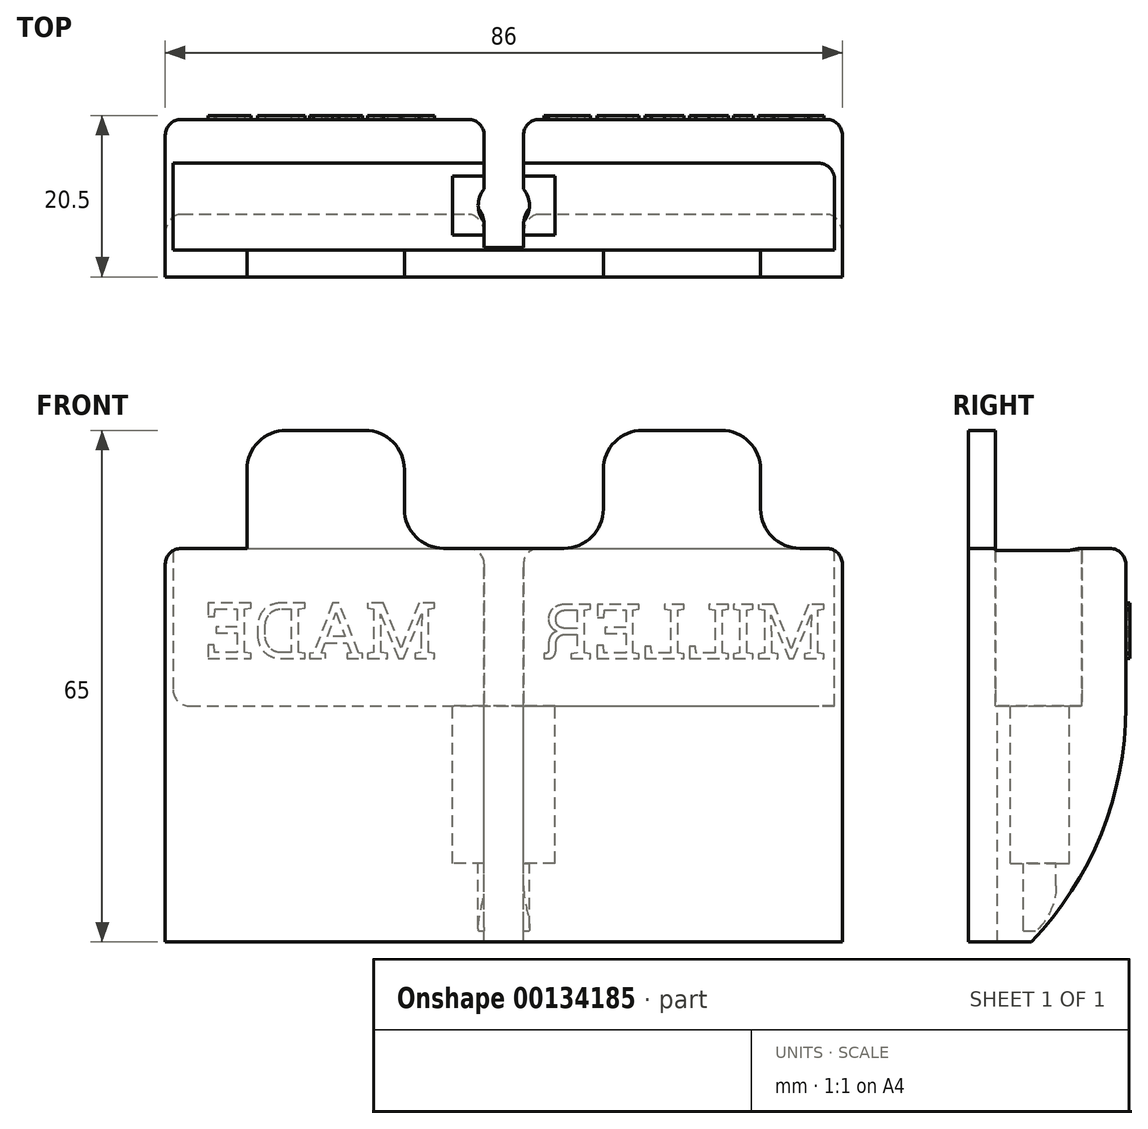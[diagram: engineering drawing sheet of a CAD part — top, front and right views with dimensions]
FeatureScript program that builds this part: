
annotation { "Feature Type Name" : "Feature", "Feature Type Description" : "" }
export const myFeature = defineFeature(function(context is Context, id is Id, definition is map)
    precondition{}
    {
        {
            var Q0;
            Q0=qCreatedBy(makeId("Top.planeOp"),FACE);
            var sketch = newSketch(context, id + "F0", { "sketchPlane" : qUnion([Q0])});
            skLineSegment(sketch, "E0.bottom", {"start": v(0, 0) * mm, "end": v(83, 0) * mm});
            skLineSegment(sketch, "E0.top", {"start": v(0, 20) * mm, "end": v(83, 20) * mm});
            skLineSegment(sketch, "E0.left", {"start": v(0, 0) * mm, "end": v(0, 20) * mm});
            skLineSegment(sketch, "E0.right", {"start": v(83, 0) * mm, "end": v(83, 20) * mm});
            skLineSegment(sketch, "E1.bottom", {"start": v(0, 5.2) * mm, "end": v(83, 5.2) * mm});
            skLineSegment(sketch, "E1.top", {"start": v(0, 16.2) * mm, "end": v(83, 16.2) * mm});
            skLineSegment(sketch, "E1.left", {"start": v(0, 5.2) * mm, "end": v(0, 16.2) * mm});
            skLineSegment(sketch, "E1.right", {"start": v(83, 5.2) * mm, "end": v(83, 16.2) * mm});
            skSolve(sketch);
        }
        {
            var Q0;
            {var subQ0=sQuery(id+"F0.wireOp",EDGE,"E0.bottom");Q0=makeQuery(id+"F0.imprint","IMPRINT",FACE,{"disambiguationData":[TD([[makeQuery(id+"F0.imprint","IMPRINT",EDGE,{"derivedFrom":subQ0}),1.0]])]});}
            var Q1;
            {var subQ0=sQuery(id+"F0.wireOp",EDGE,"E0.top");Q1=makeQuery(id+"F0.imprint","IMPRINT",FACE,{"disambiguationData":[TD([[makeQuery(id+"F0.imprint","IMPRINT",EDGE,{"derivedFrom":subQ0}),-1.0]])]});}
            var Q2;
            Q2=makeQuery(id+"F0.imprint","IMPRINT",FACE,{"disambiguationData":[TD([[makeQuery(id+"F0.imprint","IMPRINT",EDGE,{"derivedFrom":sQuery(id+"F0.wireOp",EDGE,"E1.bottom")}),1.0]])]});
            extrude(context, id + "F1", {"entities" : qUnion([Q0, Q1, Q2]), "depth" : 30 * mm});
        }
        {
            var Q0;
            Q0=makeQuery(id+"F1.opExtrude","CAP_FACE",FACE,{"disambiguationData":[OSD([sQuery(id+"F0.wireOp",EDGE,"E0.bottom"),sQuery(id+"F0.wireOp",EDGE,"E0.top"),sQuery(id+"F0.wireOp",EDGE,"E0.left"),sQuery(id+"F0.wireOp",EDGE,"E0.right"),sQuery(id+"F0.wireOp",EDGE,"E1.left"),sQuery(id+"F0.wireOp",EDGE,"E1.right")])],"isStart":false});
            var sketch = newSketch(context, id + "F2", { "sketchPlane" : qUnion([Q0])});
            skLineSegment(sketch, "E2.bottom", {"start": v(0, 3.43) * mm, "end": v(83, 3.43) * mm});
            skLineSegment(sketch, "E2.top", {"start": v(0, 14.43) * mm, "end": v(83, 14.43) * mm});
            skLineSegment(sketch, "E2.left", {"start": v(0, 3.43) * mm, "end": v(0, 14.43) * mm});
            skLineSegment(sketch, "E2.right", {"start": v(83, 3.43) * mm, "end": v(83, 14.43) * mm});
            skSolve(sketch);
        }
        {
            var Q0;
            Q0=makeQuery(id+"F2.imprint","IMPRINT",FACE,{"disambiguationData":[TD([[makeQuery(id+"F2.imprint","IMPRINT",EDGE,{"derivedFrom":sQuery(id+"F2.wireOp",EDGE,"E2.bottom")}),1.0]])]});
            extrude(context, id + "F3", {"entities" : qUnion([Q0]), "operationType" : NewBodyOperationType.REMOVE, "oppositeDirection" : true, "depth" : 15 * mm});
        }
        {
            var Q0;
            {var subQ0=sQuery(id+"F0.wireOp",EDGE,"E0.top");var subQ1=sQuery(id+"F0.wireOp",EDGE,"E1.left");var subQ2=sQuery(id+"F0.wireOp",EDGE,"E0.left");var subQ3=sQuery(id+"F0.wireOp",EDGE,"E1.right");var subQ4=sQuery(id+"F0.wireOp",EDGE,"E0.right");Q0=makeQuery(id+"F3.boolean.opBoolean","SPLIT",FACE,{"disambiguationData":[TD([makeQuery(id+"F1.opExtrude","SWEPT_FACE",FACE,{"disambiguationData":[OSD([subQ0])]})])],"derivedFrom":makeQuery(id+"F1.opExtrude","CAP_FACE",FACE,{"disambiguationData":[OSD([sQuery(id+"F0.wireOp",EDGE,"E0.bottom"),subQ0,subQ2,subQ4,subQ1,subQ3])],"isStart":false})});}
            var sketch = newSketch(context, id + "F4", { "sketchPlane" : qUnion([Q0])});
            skLineSegment(sketch, "E3", {"start": v(41.5, 20) * mm, "end": v(41.5, -12.57) * mm, "construction": true});
            skLineSegment(sketch, "E4.bottom", {"start": v(44, 3.71) * mm, "end": v(39, 3.71) * mm});
            skLineSegment(sketch, "E4.top", {"start": v(44, 36.29) * mm, "end": v(39, 36.29) * mm});
            skLineSegment(sketch, "E4.left", {"start": v(44, 3.71) * mm, "end": v(44, 36.29) * mm});
            skLineSegment(sketch, "E4.right", {"start": v(39, 3.71) * mm, "end": v(39, 36.29) * mm});
            skPoint(sketch, "E4.middle", {"position": v(41.5, 20) * mm});
            skPoint(sketch, "E4.cornerSnap0", {"position": v(41.5, 3.71) * mm});
            skSolve(sketch);
        }
        {
            var Q0;
            {var subQ0=sQuery(id+"F4.wireOp",EDGE,"E4.bottom");Q0=makeQuery(id+"F4.imprint","IMPRINT",FACE,{"disambiguationData":[TD([[makeQuery(id+"F4.imprint","IMPRINT",EDGE,{"derivedFrom":subQ0}),-1.0]])]});}
            var Q1;
            {var subQ0=sQuery(id+"F4.wireOp",EDGE,"E4.left");var subQ1=makeQuery(id+"F3.boolean.opBoolean","COPY",EDGE,{"derivedFrom":makeQuery(id+"F3.opExtrude","CAP_EDGE",EDGE,{"disambiguationData":[OSD([sQuery(id+"F2.wireOp",EDGE,"E2.top")])],"isStart":true})});var subQ2=makeQuery(id+"F4.imprint","INTERSECT",VERTEX,{"derivedFrom":[subQ1,subQ0]});Q1=makeQuery(id+"F4.imprint","IMPRINT",FACE,{"disambiguationData":[TD([[makeQuery(id+"F4.imprint","IMPRINT",EDGE,{"disambiguationData":[TD([[subQ2,-1.0]])],"derivedFrom":subQ0}),1.0]])]});}
            var Q2;
            {var subQ0=sQuery(id+"F4.wireOp",EDGE,"E4.top");Q2=makeQuery(id+"F4.imprint","IMPRINT",FACE,{"disambiguationData":[TD([[makeQuery(id+"F4.imprint","IMPRINT",EDGE,{"derivedFrom":subQ0}),1.0]])]});}
            extrude(context, id + "F5", {"entities" : qUnion([Q0, Q1, Q2]), "operationType" : NewBodyOperationType.REMOVE, "oppositeDirection" : true, "depth" : 77.48 * mm});
        }
        {
            var Q0;
            Q0=makeQuery(id+"F3.boolean.opBoolean","COPY",FACE,{"derivedFrom":makeQuery(id+"F3.opExtrude","CAP_FACE",FACE,{"disambiguationData":[OSD([sQuery(id+"F2.wireOp",EDGE,"E2.bottom"),sQuery(id+"F2.wireOp",EDGE,"E2.top"),sQuery(id+"F2.wireOp",EDGE,"E2.left"),sQuery(id+"F2.wireOp",EDGE,"E2.right")])],"isStart":false})});
            var sketch = newSketch(context, id + "F6", { "sketchPlane" : qUnion([Q0])});
            skLineSegment(sketch, "E5", {"start": v(44, 14.43) * mm, "end": v(39, 14.43) * mm, "construction": true});
            skLineSegment(sketch, "E6", {"start": v(41.5, 14.43) * mm, "end": v(41.5, 3.71) * mm, "construction": true});
            skLineSegment(sketch, "E7.bottom", {"start": v(48, 5.32) * mm, "end": v(35, 5.32) * mm});
            skLineSegment(sketch, "E7.top", {"start": v(48, 12.82) * mm, "end": v(35, 12.82) * mm});
            skLineSegment(sketch, "E7.left", {"start": v(48, 5.32) * mm, "end": v(48, 12.82) * mm});
            skLineSegment(sketch, "E7.right", {"start": v(35, 5.32) * mm, "end": v(35, 12.82) * mm});
            skPoint(sketch, "E7.middle", {"position": v(41.5, 9.07) * mm});
            skSolve(sketch);
        }
        {
            var Q0;
            Q0=makeQuery(id+"F1.opExtrude","CAP_FACE",FACE,{"disambiguationData":[OSD([sQuery(id+"F0.wireOp",EDGE,"E0.bottom"),sQuery(id+"F0.wireOp",EDGE,"E0.top"),sQuery(id+"F0.wireOp",EDGE,"E0.left"),sQuery(id+"F0.wireOp",EDGE,"E0.right"),sQuery(id+"F0.wireOp",EDGE,"E1.left"),sQuery(id+"F0.wireOp",EDGE,"E1.right")])],"isStart":true});
            extrude(context, id + "F7", {"entities" : qUnion([Q0]), "operationType" : NewBodyOperationType.ADD, "depth" : 15 * mm});
        }
        {
            var Q0;
            {var subQ0=sQuery(id+"F6.wireOp",EDGE,"E7.left");Q0=makeQuery(id+"F6.imprint","IMPRINT",FACE,{"disambiguationData":[TD([[makeQuery(id+"F6.imprint","IMPRINT",EDGE,{"derivedFrom":subQ0}),1.0]])]});}
            var Q1;
            {var subQ0=sQuery(id+"F6.wireOp",EDGE,"E7.right");Q1=makeQuery(id+"F6.imprint","IMPRINT",FACE,{"disambiguationData":[TD([[makeQuery(id+"F6.imprint","IMPRINT",EDGE,{"derivedFrom":subQ0}),-1.0]])]});}
            extrude(context, id + "F8", {"entities" : qUnion([Q0, Q1]), "operationType" : NewBodyOperationType.REMOVE, "oppositeDirection" : true, "depth" : 20 * mm});
        }
        {
            var Q0;
            {var subQ2=sQuery(id+"F0.wireOp",EDGE,"E0.top");Q0=makeQuery(id+"F7.opExtrude","CAP_EDGE",EDGE,{"disambiguationData":[OSD([subQ2]),TDD([makeQuery(id+"F5.boolean.opBoolean","SPLIT",EDGE,{"disambiguationData":[TD([makeQuery(id+"F5.opExtrude","SWEPT_FACE",FACE,{"disambiguationData":[OSD([sQuery(id+"F4.wireOp",EDGE,"E4.left")])]})])],"derivedFrom":makeQuery(id+"F1.opExtrude","CAP_EDGE",EDGE,{"disambiguationData":[OSD([subQ2])],"isStart":true})})])],"isStart":false});}
            var Q1;
            {var subQ2=sQuery(id+"F0.wireOp",EDGE,"E0.top");Q1=makeQuery(id+"F7.opExtrude","CAP_EDGE",EDGE,{"disambiguationData":[OSD([subQ2]),TDD([makeQuery(id+"F5.boolean.opBoolean","SPLIT",EDGE,{"disambiguationData":[TD([makeQuery(id+"F5.opExtrude","SWEPT_FACE",FACE,{"disambiguationData":[OSD([sQuery(id+"F4.wireOp",EDGE,"E4.right")])]})])],"derivedFrom":makeQuery(id+"F1.opExtrude","CAP_EDGE",EDGE,{"disambiguationData":[OSD([subQ2])],"isStart":true})})])],"isStart":false});}
            chamfer(context, id + "F9", {"entities" : qUnion([Q0, Q1]), "width" : 12 * mm, "tangentPropagation" : true});
        }
        {
            var Q0;
            {var subQ4=sQuery(id+"F0.wireOp",EDGE,"E0.top");var subQ7=makeQuery(id+"F1.opExtrude","SWEPT_FACE",FACE,{"disambiguationData":[OSD([subQ4])]});var subQ9=makeQuery(id+"F5.opExtrude","SWEPT_FACE",FACE,{"disambiguationData":[OSD([sQuery(id+"F4.wireOp",EDGE,"E4.left")])]});var subQ10=makeQuery(id+"F5.boolean.opBoolean","SPLIT",EDGE,{"disambiguationData":[TD([subQ9])],"derivedFrom":makeQuery(id+"F1.opExtrude","CAP_EDGE",EDGE,{"disambiguationData":[OSD([subQ4])],"isStart":true})});Q0=makeQuery(id+"F9.opChamfer","BLEND_EDGE",EDGE,{"blendedFrom":[makeQuery(id+"F7.opExtrude","CAP_EDGE",EDGE,{"disambiguationData":[OSD([subQ4]),TDD([subQ10])],"isStart":false}),makeQuery(id+"F7.boolean.opBoolean","MERGE",FACE,{"derivedFrom":[makeQuery(id+"F5.boolean.opBoolean","SPLIT",FACE,{"disambiguationData":[TD([subQ9])],"derivedFrom":subQ7}),makeQuery(id+"F7.opExtrude","SWEPT_FACE",FACE,{"disambiguationData":[OSD([subQ4]),TDD([subQ10])]})]})],"blendedInto":[makeQuery(id+"F7.boolean.opBoolean","MERGE",FACE,{"derivedFrom":[makeQuery(id+"F5.boolean.opBoolean","SPLIT",FACE,{"disambiguationData":[TD([subQ9])],"derivedFrom":subQ7}),makeQuery(id+"F7.opExtrude","SWEPT_FACE",FACE,{"disambiguationData":[OSD([subQ4]),TDD([subQ10])]})]})]});}
            var Q1;
            {var subQ4=sQuery(id+"F0.wireOp",EDGE,"E0.top");var subQ7=makeQuery(id+"F1.opExtrude","SWEPT_FACE",FACE,{"disambiguationData":[OSD([subQ4])]});var subQ9=makeQuery(id+"F5.opExtrude","SWEPT_FACE",FACE,{"disambiguationData":[OSD([sQuery(id+"F4.wireOp",EDGE,"E4.right")])]});var subQ10=makeQuery(id+"F5.boolean.opBoolean","SPLIT",EDGE,{"disambiguationData":[TD([subQ9])],"derivedFrom":makeQuery(id+"F1.opExtrude","CAP_EDGE",EDGE,{"disambiguationData":[OSD([subQ4])],"isStart":true})});Q1=makeQuery(id+"F9.opChamfer","BLEND_EDGE",EDGE,{"blendedFrom":[makeQuery(id+"F7.opExtrude","CAP_EDGE",EDGE,{"disambiguationData":[OSD([subQ4]),TDD([subQ10])],"isStart":false}),makeQuery(id+"F7.boolean.opBoolean","MERGE",FACE,{"derivedFrom":[makeQuery(id+"F5.boolean.opBoolean","SPLIT",FACE,{"disambiguationData":[TD([subQ9])],"derivedFrom":subQ7}),makeQuery(id+"F7.opExtrude","SWEPT_FACE",FACE,{"disambiguationData":[OSD([subQ4]),TDD([subQ10])]})]})],"blendedInto":[makeQuery(id+"F7.boolean.opBoolean","MERGE",FACE,{"derivedFrom":[makeQuery(id+"F5.boolean.opBoolean","SPLIT",FACE,{"disambiguationData":[TD([subQ9])],"derivedFrom":subQ7}),makeQuery(id+"F7.opExtrude","SWEPT_FACE",FACE,{"disambiguationData":[OSD([subQ4]),TDD([subQ10])]})]})]});}
            fillet(context, id + "F10", {"entities" : qUnion([Q0, Q1]), "radius" : 42.96 * mm, "tangentPropagation" : true, "allowEdgeOverflow" : false});
        }
        {
            var Q0;
            {var subQ4=sQuery(id+"F0.wireOp",EDGE,"E0.top");var subQ7=makeQuery(id+"F1.opExtrude","SWEPT_FACE",FACE,{"disambiguationData":[OSD([subQ4])]});var subQ9=makeQuery(id+"F5.opExtrude","SWEPT_FACE",FACE,{"disambiguationData":[OSD([sQuery(id+"F4.wireOp",EDGE,"E4.left")])]});Q0=makeQuery(id+"F7.boolean.opBoolean","MERGE",FACE,{"derivedFrom":[makeQuery(id+"F5.boolean.opBoolean","SPLIT",FACE,{"disambiguationData":[TD([subQ9])],"derivedFrom":subQ7}),makeQuery(id+"F7.opExtrude","SWEPT_FACE",FACE,{"disambiguationData":[OSD([subQ4]),TDD([makeQuery(id+"F5.boolean.opBoolean","SPLIT",EDGE,{"disambiguationData":[TD([subQ9])],"derivedFrom":makeQuery(id+"F1.opExtrude","CAP_EDGE",EDGE,{"disambiguationData":[OSD([subQ4])],"isStart":true})})])]})]});}
            var sketch = newSketch(context, id + "F11", { "sketchPlane" : qUnion([Q0])});
            skText(sketch, "E8", { "text": "MILLER", "fontName": "Arimo-Regular.ttf"});
            skPoint(sketch, "E9", {"position": v(-63.5, 30) * mm});
            skText(sketch, "E10", { "text": "MADE", "fontName": "DroidSansMono.ttf"});
            const initialGuessF11  = {"E8": [-0.07876, 0.02007, 1, 0, 0.00604], "E10": [-0.03074, 0.02007, 1, 0, 0.00604]};
            skSetInitialGuess(sketch, initialGuessF11);
            skSolve(sketch);
        }
        {
            var Q0;
            Q0 = qSketchRegion(id + "F11", true);
            extrude(context, id + "F12", {"entities" : qUnion([Q0]), "operationType" : NewBodyOperationType.ADD, "oppositeDirection" : true, "depth" : 1 * mm});
        }
        {
            var Q0;
            {var subQ0=sQuery(id+"F0.wireOp",EDGE,"E0.bottom");var subQ1=sQuery(id+"F0.wireOp",EDGE,"E1.left");var subQ2=sQuery(id+"F0.wireOp",EDGE,"E0.left");var subQ3=sQuery(id+"F0.wireOp",EDGE,"E1.right");var subQ4=sQuery(id+"F0.wireOp",EDGE,"E0.right");Q0=makeQuery(id+"F3.boolean.opBoolean","SPLIT",FACE,{"disambiguationData":[TD([makeQuery(id+"F1.opExtrude","SWEPT_FACE",FACE,{"disambiguationData":[OSD([subQ0])]})])],"derivedFrom":makeQuery(id+"F1.opExtrude","CAP_FACE",FACE,{"disambiguationData":[OSD([subQ0,sQuery(id+"F0.wireOp",EDGE,"E0.top"),subQ2,subQ4,subQ1,subQ3])],"isStart":false})});}
            var Q1;
            {var subQ0=sQuery(id+"F0.wireOp",EDGE,"E0.top");var subQ1=makeQuery(id+"F1.opExtrude","SWEPT_FACE",FACE,{"disambiguationData":[OSD([subQ0])]});var subQ2=sQuery(id+"F0.wireOp",EDGE,"E1.right");var subQ3=sQuery(id+"F0.wireOp",EDGE,"E0.right");var subQ6=sQuery(id+"F0.wireOp",EDGE,"E1.left");var subQ7=sQuery(id+"F0.wireOp",EDGE,"E0.left");Q1=makeQuery(id+"F5.boolean.opBoolean","SPLIT",FACE,{"disambiguationData":[TD([makeQuery(id+"F5.opExtrude","SWEPT_FACE",FACE,{"disambiguationData":[OSD([sQuery(id+"F4.wireOp",EDGE,"E4.left")])]})])],"derivedFrom":makeQuery(id+"F3.boolean.opBoolean","SPLIT",FACE,{"disambiguationData":[TD([subQ1])],"derivedFrom":makeQuery(id+"F1.opExtrude","CAP_FACE",FACE,{"disambiguationData":[OSD([sQuery(id+"F0.wireOp",EDGE,"E0.bottom"),subQ0,subQ7,subQ3,subQ6,subQ2])],"isStart":false})})});}
            var Q2;
            {var subQ0=sQuery(id+"F0.wireOp",EDGE,"E0.top");var subQ1=makeQuery(id+"F1.opExtrude","SWEPT_FACE",FACE,{"disambiguationData":[OSD([subQ0])]});var subQ2=sQuery(id+"F0.wireOp",EDGE,"E1.left");var subQ3=sQuery(id+"F0.wireOp",EDGE,"E0.left");var subQ6=sQuery(id+"F0.wireOp",EDGE,"E1.right");var subQ7=sQuery(id+"F0.wireOp",EDGE,"E0.right");Q2=makeQuery(id+"F5.boolean.opBoolean","SPLIT",FACE,{"disambiguationData":[TD([makeQuery(id+"F5.opExtrude","SWEPT_FACE",FACE,{"disambiguationData":[OSD([sQuery(id+"F4.wireOp",EDGE,"E4.right")])]})])],"derivedFrom":makeQuery(id+"F3.boolean.opBoolean","SPLIT",FACE,{"disambiguationData":[TD([subQ1])],"derivedFrom":makeQuery(id+"F1.opExtrude","CAP_FACE",FACE,{"disambiguationData":[OSD([sQuery(id+"F0.wireOp",EDGE,"E0.bottom"),subQ0,subQ3,subQ7,subQ2,subQ6])],"isStart":false})})});}
            extrude(context, id + "F13", {"entities" : qUnion([Q0, Q1, Q2]), "operationType" : NewBodyOperationType.ADD, "depth" : 5 * mm});
        }
        {
            var Q0;
            Q0=makeQuery(id+"F8.boolean.opBoolean","COPY",FACE,{"derivedFrom":makeQuery(id+"F8.opExtrude","CAP_FACE",FACE,{"disambiguationData":[OSD([sQuery(id+"F2.wireOp",EDGE,"E2.bottom"),sQuery(id+"F2.wireOp",EDGE,"E2.top"),sQuery(id+"F2.wireOp",EDGE,"E2.left"),sQuery(id+"F2.wireOp",EDGE,"E2.right"),sQuery(id+"F4.wireOp",EDGE,"E4.left"),sQuery(id+"F6.wireOp",EDGE,"E7.bottom"),sQuery(id+"F6.wireOp",EDGE,"E7.top"),sQuery(id+"F6.wireOp",EDGE,"E7.left")])],"isStart":false})});
            var sketch = newSketch(context, id + "F14", { "sketchPlane" : qUnion([Q0])});
            skLineSegment(sketch, "E11", {"start": v(48, 9.07) * mm, "end": v(35, 9.07) * mm, "construction": true});
            skCircle(sketch, "E12", {"center": v(41.5, 9.07) * mm, "radius": 3.25 * mm});
            skSolve(sketch);
        }
        {
            var Q0;
            {var subQ0=sQuery(id+"F14.wireOp",EDGE,"E12");var subQ1=makeQuery(id+"F8.boolean.opBoolean","COPY",EDGE,{"derivedFrom":makeQuery(id+"F8.opExtrude","CAP_EDGE",EDGE,{"disambiguationData":[OSD([sQuery(id+"F2.wireOp",EDGE,"E2.bottom"),sQuery(id+"F2.wireOp",EDGE,"E2.top"),sQuery(id+"F2.wireOp",EDGE,"E2.left"),sQuery(id+"F2.wireOp",EDGE,"E2.right"),sQuery(id+"F4.wireOp",EDGE,"E4.left")])],"isStart":false})});var subQ2=makeQuery(id+"F14.imprint","INTERSECT",VERTEX,{"disambiguationData":[OD(0.0)],"derivedFrom":[subQ1,subQ0]});Q0=makeQuery(id+"F14.imprint","IMPRINT",FACE,{"disambiguationData":[TD([[makeQuery(id+"F14.imprint","IMPRINT",EDGE,{"disambiguationData":[TD([[subQ2,-1.0]])],"derivedFrom":subQ0}),1.0]])]});}
            var Q1;
            {var subQ0=sQuery(id+"F14.wireOp",EDGE,"E12");var subQ1=makeQuery(id+"F8.boolean.opBoolean","COPY",EDGE,{"derivedFrom":makeQuery(id+"F8.opExtrude","CAP_EDGE",EDGE,{"disambiguationData":[OSD([sQuery(id+"F2.wireOp",EDGE,"E2.bottom"),sQuery(id+"F2.wireOp",EDGE,"E2.top"),sQuery(id+"F2.wireOp",EDGE,"E2.left"),sQuery(id+"F2.wireOp",EDGE,"E2.right"),sQuery(id+"F4.wireOp",EDGE,"E4.left")])],"isStart":false})});var subQ2=makeQuery(id+"F14.imprint","INTERSECT",VERTEX,{"disambiguationData":[OD(0.0)],"derivedFrom":[subQ1,subQ0]});Q1=makeQuery(id+"F14.imprint","IMPRINT",FACE,{"disambiguationData":[TD([[makeQuery(id+"F14.imprint","IMPRINT",EDGE,{"disambiguationData":[TD([[subQ2,1.0]])],"derivedFrom":subQ0}),1.0]])]});}
            extrude(context, id + "F15", {"entities" : qUnion([Q0, Q1]), "operationType" : NewBodyOperationType.REMOVE, "oppositeDirection" : true, "depth" : 8.6 * mm});
        }
        {
            var Q0;
            {var subQ0=sQuery(id+"F0.wireOp",EDGE,"E1.right");var subQ1=sQuery(id+"F0.wireOp",EDGE,"E0.right");var subQ2=sQuery(id+"F0.wireOp",EDGE,"E0.top");var subQ3=sQuery(id+"F0.wireOp",EDGE,"E0.bottom");var subQ5=makeQuery(id+"F1.opExtrude","SWEPT_FACE",FACE,{"disambiguationData":[OSD([subQ1,subQ0])]});var subQ6=makeQuery(id+"F1.opExtrude","CAP_EDGE",EDGE,{"disambiguationData":[OSD([subQ1,subQ0])],"isStart":false});Q0=makeQuery(id+"F13.boolean.opBoolean","MERGE",FACE,{"derivedFrom":[makeQuery(id+"F7.boolean.opBoolean","MERGE",FACE,{"derivedFrom":[subQ5,makeQuery(id+"F7.opExtrude","SWEPT_FACE",FACE,{"disambiguationData":[OSD([subQ1,subQ0])]})]}),makeQuery(id+"F13.opExtrude","SWEPT_FACE",FACE,{"disambiguationData":[OSD([subQ1,subQ0]),TDD([makeQuery(id+"F3.boolean.opBoolean","SPLIT",EDGE,{"disambiguationData":[TD([makeQuery(id+"F1.opExtrude","SWEPT_FACE",FACE,{"disambiguationData":[OSD([subQ3])]})])],"derivedFrom":subQ6})])]}),makeQuery(id+"F13.opExtrude","SWEPT_FACE",FACE,{"disambiguationData":[OSD([subQ1,subQ0]),TDD([makeQuery(id+"F3.boolean.opBoolean","SPLIT",EDGE,{"disambiguationData":[TD([makeQuery(id+"F1.opExtrude","SWEPT_FACE",FACE,{"disambiguationData":[OSD([subQ2])]})])],"derivedFrom":subQ6})])]})]});}
            extrude(context, id + "F16", {"entities" : qUnion([Q0]), "operationType" : NewBodyOperationType.ADD, "depth" : .5 * mm});
        }
        {
            var Q0;
            {var subQ0=sQuery(id+"F0.wireOp",EDGE,"E1.left");var subQ1=sQuery(id+"F0.wireOp",EDGE,"E0.left");var subQ2=sQuery(id+"F0.wireOp",EDGE,"E0.top");var subQ3=sQuery(id+"F0.wireOp",EDGE,"E0.bottom");var subQ5=makeQuery(id+"F1.opExtrude","SWEPT_FACE",FACE,{"disambiguationData":[OSD([subQ1,subQ0])]});var subQ6=makeQuery(id+"F1.opExtrude","CAP_EDGE",EDGE,{"disambiguationData":[OSD([subQ1,subQ0])],"isStart":false});Q0=makeQuery(id+"F13.boolean.opBoolean","MERGE",FACE,{"derivedFrom":[makeQuery(id+"F7.boolean.opBoolean","MERGE",FACE,{"derivedFrom":[subQ5,makeQuery(id+"F7.opExtrude","SWEPT_FACE",FACE,{"disambiguationData":[OSD([subQ1,subQ0])]})]}),makeQuery(id+"F13.opExtrude","SWEPT_FACE",FACE,{"disambiguationData":[OSD([subQ1,subQ0]),TDD([makeQuery(id+"F3.boolean.opBoolean","SPLIT",EDGE,{"disambiguationData":[TD([makeQuery(id+"F1.opExtrude","SWEPT_FACE",FACE,{"disambiguationData":[OSD([subQ3])]})])],"derivedFrom":subQ6})])]}),makeQuery(id+"F13.opExtrude","SWEPT_FACE",FACE,{"disambiguationData":[OSD([subQ1,subQ0]),TDD([makeQuery(id+"F3.boolean.opBoolean","SPLIT",EDGE,{"disambiguationData":[TD([makeQuery(id+"F1.opExtrude","SWEPT_FACE",FACE,{"disambiguationData":[OSD([subQ2])]})])],"derivedFrom":subQ6})])]})]});}
            extrude(context, id + "F17", {"entities" : qUnion([Q0]), "operationType" : NewBodyOperationType.ADD, "depth" : .5 * mm});
        }
        {
            var Q0;
            Q0=makeQuery(id+"F16.opExtrude","CAP_FACE",FACE,{"disambiguationData":[OSD([sQuery(id+"F0.wireOp",EDGE,"E0.right"),sQuery(id+"F0.wireOp",EDGE,"E1.right")])],"isStart":false});
            var sketch = newSketch(context, id + "F18", { "sketchPlane" : qUnion([Q0])});
            skLineSegment(sketch, "E13.bottom", {"start": v(3.43, 35) * mm, "end": v(14.43, 35) * mm});
            skLineSegment(sketch, "E13.top", {"start": v(3.43, 15) * mm, "end": v(14.43, 15) * mm});
            skLineSegment(sketch, "E13.left", {"start": v(3.43, 35) * mm, "end": v(3.43, 15) * mm});
            skLineSegment(sketch, "E13.right", {"start": v(14.43, 35) * mm, "end": v(14.43, 15) * mm});
            skSolve(sketch);
        }
        {
            var Q0;
            Q0 = qSketchRegion(id + "F18", true);
            extrude(context, id + "F19", {"entities" : qUnion([Q0]), "depth" : 1 * mm});
        }
        {
            var Q0;
            Q0=makeQuery(id+"F19.opExtrude","SWEPT_BODY",BODY,{"disambiguationData":[OSD([sQuery(id+"F18.wireOp",EDGE,"E13.bottom"),sQuery(id+"F18.wireOp",EDGE,"E13.top"),sQuery(id+"F18.wireOp",EDGE,"E13.left"),sQuery(id+"F18.wireOp",EDGE,"E13.right")])]});
            deleteBodies(context, id + "F20", {"entities" : qUnion([Q0])});
        }
        {
            var Q0;
            {var subQ0=sQuery(id+"F2.wireOp",EDGE,"E2.right");var subQ1=sQuery(id+"F2.wireOp",EDGE,"E2.top");var subQ2=sQuery(id+"F0.wireOp",EDGE,"E1.right");var subQ3=sQuery(id+"F0.wireOp",EDGE,"E0.right");var subQ6=makeQuery(id+"F3.boolean.opBoolean","COPY",FACE,{"derivedFrom":makeQuery(id+"F3.opExtrude","SWEPT_FACE",FACE,{"disambiguationData":[OSD([subQ1])]})});var subQ7=makeQuery(id+"F5.opExtrude","SWEPT_FACE",FACE,{"disambiguationData":[OSD([sQuery(id+"F4.wireOp",EDGE,"E4.left")])]});Q0=makeQuery(id+"F16.boolean.opBoolean","MERGE",FACE,{"derivedFrom":[makeQuery(id+"F13.boolean.opBoolean","MERGE",FACE,{"derivedFrom":[makeQuery(id+"F5.boolean.opBoolean","SPLIT",FACE,{"disambiguationData":[TD([subQ7])],"derivedFrom":subQ6}),makeQuery(id+"F13.opExtrude","SWEPT_FACE",FACE,{"disambiguationData":[OSD([subQ1]),TDD([makeQuery(id+"F5.boolean.opBoolean","SPLIT",EDGE,{"disambiguationData":[TD([subQ7])],"derivedFrom":makeQuery(id+"F3.boolean.opBoolean","COPY",EDGE,{"derivedFrom":makeQuery(id+"F3.opExtrude","CAP_EDGE",EDGE,{"disambiguationData":[OSD([subQ1])],"isStart":true})})})])]})]}),makeQuery(id+"F16.opExtrude","SWEPT_FACE",FACE,{"disambiguationData":[OSD([subQ3,subQ2,subQ1,subQ0])]})]});}
            var sketch = newSketch(context, id + "F21", { "sketchPlane" : qUnion([Q0])});
            skLineSegment(sketch, "E14.bottom", {"start": v(83.5, 15) * mm, "end": v(82.5, 15) * mm});
            skLineSegment(sketch, "E14.top", {"start": v(83.5, 35) * mm, "end": v(82.5, 35) * mm});
            skLineSegment(sketch, "E14.left", {"start": v(83.5, 15) * mm, "end": v(83.5, 35) * mm});
            skLineSegment(sketch, "E14.right", {"start": v(82.5, 15) * mm, "end": v(82.5, 35) * mm});
            skSolve(sketch);
        }
        {
            var Q0;
            Q0 = qSketchRegion(id + "F21", true);
            extrude(context, id + "F22", {"entities" : qUnion([Q0]), "operationType" : NewBodyOperationType.ADD, "depth" : 11 * mm});
        }
        {
            var Q0;
            {var subQ0=sQuery(id+"F2.wireOp",EDGE,"E2.bottom");Q0=makeQuery(id+"F17.boolean.opBoolean","MERGE",FACE,{"derivedFrom":[makeQuery(id+"F16.boolean.opBoolean","MERGE",FACE,{"derivedFrom":[makeQuery(id+"F13.boolean.opBoolean","MERGE",FACE,{"derivedFrom":[makeQuery(id+"F3.boolean.opBoolean","COPY",FACE,{"derivedFrom":makeQuery(id+"F3.opExtrude","SWEPT_FACE",FACE,{"disambiguationData":[OSD([subQ0])]})}),makeQuery(id+"F13.opExtrude","SWEPT_FACE",FACE,{"disambiguationData":[OSD([subQ0])]})]}),makeQuery(id+"F16.opExtrude","SWEPT_FACE",FACE,{"disambiguationData":[OSD([sQuery(id+"F0.wireOp",EDGE,"E0.right"),sQuery(id+"F0.wireOp",EDGE,"E1.right"),subQ0,sQuery(id+"F2.wireOp",EDGE,"E2.right")])]})]}),makeQuery(id+"F17.opExtrude","SWEPT_FACE",FACE,{"disambiguationData":[OSD([sQuery(id+"F0.wireOp",EDGE,"E0.left"),sQuery(id+"F0.wireOp",EDGE,"E1.left"),subQ0,sQuery(id+"F2.wireOp",EDGE,"E2.left")])]})]});}
            var sketch = newSketch(context, id + "F23", { "sketchPlane" : qUnion([Q0])});
            skLineSegment(sketch, "E15.bottom", {"start": v(0.5, 35) * mm, "end": v(-0.5, 35) * mm});
            skLineSegment(sketch, "E15.top", {"start": v(0.5, 15) * mm, "end": v(-0.5, 15) * mm});
            skLineSegment(sketch, "E15.left", {"start": v(0.5, 35) * mm, "end": v(0.5, 15) * mm});
            skLineSegment(sketch, "E15.right", {"start": v(-0.5, 35) * mm, "end": v(-0.5, 15) * mm});
            skSolve(sketch);
        }
        {
            var Q0;
            Q0 = qSketchRegion(id + "F23", true);
            extrude(context, id + "F24", {"entities" : qUnion([Q0]), "operationType" : NewBodyOperationType.ADD, "depth" : 11 * mm});
        }
        {
            var Q0;
            Q0=makeQuery(id+"F22.boolean.opBoolean","MERGE",FACE,{"derivedFrom":[makeQuery(id+"F16.opExtrude","CAP_FACE",FACE,{"disambiguationData":[OSD([sQuery(id+"F0.wireOp",EDGE,"E0.right"),sQuery(id+"F0.wireOp",EDGE,"E1.right")])],"isStart":false}),makeQuery(id+"F22.opExtrude","SWEPT_FACE",FACE,{"disambiguationData":[OSD([sQuery(id+"F21.wireOp",EDGE,"E14.left")])]})]});
            extrude(context, id + "F25", {"entities" : qUnion([Q0]), "operationType" : NewBodyOperationType.ADD, "depth" : 1 * mm});
        }
        {
            var Q0;
            Q0=makeQuery(id+"F24.boolean.opBoolean","MERGE",FACE,{"derivedFrom":[makeQuery(id+"F17.opExtrude","CAP_FACE",FACE,{"disambiguationData":[OSD([sQuery(id+"F0.wireOp",EDGE,"E0.left"),sQuery(id+"F0.wireOp",EDGE,"E1.left")])],"isStart":false}),makeQuery(id+"F24.opExtrude","SWEPT_FACE",FACE,{"disambiguationData":[OSD([sQuery(id+"F23.wireOp",EDGE,"E15.left")])]})]});
            extrude(context, id + "F26", {"entities" : qUnion([Q0]), "operationType" : NewBodyOperationType.ADD, "depth" : 1 * mm});
        }
        {
            var Q0;
            Q0=makeQuery(id+"F22.opExtrude","SWEPT_FACE",FACE,{"disambiguationData":[OSD([sQuery(id+"F21.wireOp",EDGE,"E14.right")])]});
            extrude(context, id + "F27", {"entities" : qUnion([Q0]), "operationType" : NewBodyOperationType.REMOVE, "oppositeDirection" : true, "depth" : 1 * mm});
        }
        {
            var Q0;
            Q0=makeQuery(id+"F24.opExtrude","SWEPT_FACE",FACE,{"disambiguationData":[OSD([sQuery(id+"F23.wireOp",EDGE,"E15.right")])]});
            extrude(context, id + "F28", {"entities" : qUnion([Q0]), "operationType" : NewBodyOperationType.REMOVE, "oppositeDirection" : true, "depth" : 1 * mm});
        }
        {
            var Q0;
            Q0=makeQuery(id+"F25.opExtrude","CAP_EDGE",EDGE,{"disambiguationData":[OSD([sQuery(id+"F0.wireOp",EDGE,"E0.right"),sQuery(id+"F0.wireOp",EDGE,"E1.right"),sQuery(id+"F21.wireOp",EDGE,"E14.top"),sQuery(id+"F21.wireOp",EDGE,"E14.left")])],"isStart":false});
            var Q1;
            Q1=makeQuery(id+"F26.opExtrude","CAP_EDGE",EDGE,{"disambiguationData":[OSD([sQuery(id+"F0.wireOp",EDGE,"E0.left"),sQuery(id+"F0.wireOp",EDGE,"E1.left"),sQuery(id+"F23.wireOp",EDGE,"E15.bottom"),sQuery(id+"F23.wireOp",EDGE,"E15.left")])],"isStart":false});
            var Q2;
            Q2=makeQuery(id+"F13.opExtrude","CAP_EDGE",EDGE,{"disambiguationData":[OSD([sQuery(id+"F4.wireOp",EDGE,"E4.left")])],"isStart":false});
            var Q3;
            Q3=makeQuery(id+"F13.opExtrude","CAP_EDGE",EDGE,{"disambiguationData":[OSD([sQuery(id+"F4.wireOp",EDGE,"E4.right")])],"isStart":false});
            fillet(context, id + "F29", {"entities" : qUnion([Q0, Q1, Q2, Q3]), "radius" : 2 * mm, "tangentPropagation" : true, "allowEdgeOverflow" : false});
        }
        {
            var Q0;
            Q0=makeQuery(id+"F25.opExtrude","CAP_EDGE",EDGE,{"disambiguationData":[OSD([sQuery(id+"F0.wireOp",EDGE,"E0.top"),sQuery(id+"F0.wireOp",EDGE,"E0.right")])],"isStart":false});
            var Q1;
            Q1=makeQuery(id+"F25.opExtrude","CAP_EDGE",EDGE,{"disambiguationData":[OSD([sQuery(id+"F0.wireOp",EDGE,"E0.top"),sQuery(id+"F0.wireOp",EDGE,"E0.right"),sQuery(id+"F0.wireOp",EDGE,"E1.right")])],"isStart":false});
            var Q2;
            Q2=makeQuery(id+"F26.opExtrude","CAP_EDGE",EDGE,{"disambiguationData":[OSD([sQuery(id+"F0.wireOp",EDGE,"E0.top"),sQuery(id+"F0.wireOp",EDGE,"E0.left")])],"isStart":false});
            var Q3;
            Q3=makeQuery(id+"F26.opExtrude","CAP_EDGE",EDGE,{"disambiguationData":[OSD([sQuery(id+"F0.wireOp",EDGE,"E0.top"),sQuery(id+"F0.wireOp",EDGE,"E0.left"),sQuery(id+"F0.wireOp",EDGE,"E1.left")])],"isStart":false});
            fillet(context, id + "F30", {"entities" : qUnion([Q0, Q1, Q2, Q3]), "radius" : 2 * mm, "tangentPropagation" : true, "allowEdgeOverflow" : false});
        }
        {
            var Q0;
            Q0=makeQuery(id+"F27.boolean.opBoolean","COPY",EDGE,{"derivedFrom":makeQuery(id+"F27.opExtrude","CAP_EDGE",EDGE,{"disambiguationData":[OSD([sQuery(id+"F0.wireOp",EDGE,"E0.right"),sQuery(id+"F0.wireOp",EDGE,"E1.right"),sQuery(id+"F2.wireOp",EDGE,"E2.top"),sQuery(id+"F2.wireOp",EDGE,"E2.right"),sQuery(id+"F21.wireOp",EDGE,"E14.bottom"),sQuery(id+"F21.wireOp",EDGE,"E14.right")])],"isStart":false})});
            var Q1;
            Q1=makeQuery(id+"F28.boolean.opBoolean","COPY",EDGE,{"derivedFrom":makeQuery(id+"F28.opExtrude","CAP_EDGE",EDGE,{"disambiguationData":[OSD([sQuery(id+"F0.wireOp",EDGE,"E0.left"),sQuery(id+"F0.wireOp",EDGE,"E0.right"),sQuery(id+"F0.wireOp",EDGE,"E1.left"),sQuery(id+"F0.wireOp",EDGE,"E1.right"),sQuery(id+"F2.wireOp",EDGE,"E2.bottom"),sQuery(id+"F2.wireOp",EDGE,"E2.left"),sQuery(id+"F2.wireOp",EDGE,"E2.right"),sQuery(id+"F23.wireOp",EDGE,"E15.top"),sQuery(id+"F23.wireOp",EDGE,"E15.right")])],"isStart":false})});
            fillet(context, id + "F31", {"entities" : qUnion([Q0, Q1]), "radius" : 2 * mm, "tangentPropagation" : true, "allowEdgeOverflow" : false});
        }
        {
            var Q0;
            {var subQ0=sQuery(id+"F23.wireOp",EDGE,"E15.bottom");var subQ1=sQuery(id+"F0.wireOp",EDGE,"E1.left");var subQ2=sQuery(id+"F0.wireOp",EDGE,"E0.left");var subQ3=sQuery(id+"F21.wireOp",EDGE,"E14.top");var subQ4=sQuery(id+"F0.wireOp",EDGE,"E1.right");var subQ5=sQuery(id+"F0.wireOp",EDGE,"E0.right");var subQ6=sQuery(id+"F0.wireOp",EDGE,"E0.bottom");var subQ7=makeQuery(id+"F1.opExtrude","SWEPT_FACE",FACE,{"disambiguationData":[OSD([subQ6])]});var subQ9=sQuery(id+"F0.wireOp",EDGE,"E0.top");var subQ10=makeQuery(id+"F1.opExtrude","CAP_FACE",FACE,{"disambiguationData":[OSD([subQ6,subQ9,subQ2,subQ5,subQ1,subQ4])],"isStart":false});var subQ12=makeQuery(id+"F1.opExtrude","CAP_EDGE",EDGE,{"disambiguationData":[OSD([subQ2,subQ1])],"isStart":false});var subQ14=makeQuery(id+"F1.opExtrude","CAP_EDGE",EDGE,{"disambiguationData":[OSD([subQ5,subQ4])],"isStart":false});var subQ15=makeQuery(id+"F1.opExtrude","SWEPT_FACE",FACE,{"disambiguationData":[OSD([subQ9])]});var subQ18=makeQuery(id+"F3.boolean.opBoolean","SPLIT",FACE,{"disambiguationData":[TD([subQ15])],"derivedFrom":subQ10});Q0=makeQuery(id+"F29.opFillet","SPLIT",FACE,{"disambiguationData":[OD(2.0)],"derivedFrom":makeQuery(id+"F26.boolean.opBoolean","MERGE",FACE,{"derivedFrom":[makeQuery(id+"F25.boolean.opBoolean","MERGE",FACE,{"derivedFrom":[makeQuery(id+"F24.boolean.opBoolean","MERGE",FACE,{"derivedFrom":[makeQuery(id+"F17.boolean.opBoolean","MERGE",FACE,{"derivedFrom":[makeQuery(id+"F13.opExtrude","CAP_FACE",FACE,{"disambiguationData":[OSD([subQ6,subQ9,subQ2,subQ5,subQ1,subQ4]),TDD([makeQuery(id+"F5.boolean.opBoolean","SPLIT",FACE,{"disambiguationData":[TD([makeQuery(id+"F5.opExtrude","SWEPT_FACE",FACE,{"disambiguationData":[OSD([sQuery(id+"F4.wireOp",EDGE,"E4.right")])]})])],"derivedFrom":subQ18})])],"isStart":false}),makeQuery(id+"F17.opExtrude","SWEPT_FACE",FACE,{"disambiguationData":[OSD([subQ2,subQ1]),TDD([makeQuery(id+"F13.opExtrude","CAP_EDGE",EDGE,{"disambiguationData":[OSD([subQ2,subQ1]),TDD([makeQuery(id+"F3.boolean.opBoolean","SPLIT",EDGE,{"disambiguationData":[TD([subQ15])],"derivedFrom":subQ12})])],"isStart":false})])]})]}),makeQuery(id+"F22.boolean.opBoolean","MERGE",FACE,{"derivedFrom":[makeQuery(id+"F16.boolean.opBoolean","MERGE",FACE,{"derivedFrom":[makeQuery(id+"F13.opExtrude","CAP_FACE",FACE,{"disambiguationData":[OSD([subQ6,subQ9,subQ2,subQ5,subQ1,subQ4]),TDD([makeQuery(id+"F5.boolean.opBoolean","SPLIT",FACE,{"disambiguationData":[TD([makeQuery(id+"F5.opExtrude","SWEPT_FACE",FACE,{"disambiguationData":[OSD([sQuery(id+"F4.wireOp",EDGE,"E4.left")])]})])],"derivedFrom":subQ18})])],"isStart":false}),makeQuery(id+"F16.opExtrude","SWEPT_FACE",FACE,{"disambiguationData":[OSD([subQ5,subQ4]),TDD([makeQuery(id+"F13.opExtrude","CAP_EDGE",EDGE,{"disambiguationData":[OSD([subQ5,subQ4]),TDD([makeQuery(id+"F3.boolean.opBoolean","SPLIT",EDGE,{"disambiguationData":[TD([subQ15])],"derivedFrom":subQ14})])],"isStart":false})])]})]}),makeQuery(id+"F17.boolean.opBoolean","MERGE",FACE,{"derivedFrom":[makeQuery(id+"F16.boolean.opBoolean","MERGE",FACE,{"derivedFrom":[makeQuery(id+"F13.opExtrude","CAP_FACE",FACE,{"disambiguationData":[OSD([subQ6,subQ9,subQ2,subQ5,subQ1,subQ4]),TDD([makeQuery(id+"F3.boolean.opBoolean","SPLIT",FACE,{"disambiguationData":[TD([subQ7])],"derivedFrom":subQ10})])],"isStart":false}),makeQuery(id+"F16.opExtrude","SWEPT_FACE",FACE,{"disambiguationData":[OSD([subQ5,subQ4]),TDD([makeQuery(id+"F13.opExtrude","CAP_EDGE",EDGE,{"disambiguationData":[OSD([subQ5,subQ4]),TDD([makeQuery(id+"F3.boolean.opBoolean","SPLIT",EDGE,{"disambiguationData":[TD([subQ7])],"derivedFrom":subQ14})])],"isStart":false})])]})]}),makeQuery(id+"F17.opExtrude","SWEPT_FACE",FACE,{"disambiguationData":[OSD([subQ2,subQ1]),TDD([makeQuery(id+"F13.opExtrude","CAP_EDGE",EDGE,{"disambiguationData":[OSD([subQ2,subQ1]),TDD([makeQuery(id+"F3.boolean.opBoolean","SPLIT",EDGE,{"disambiguationData":[TD([subQ7])],"derivedFrom":subQ12})])],"isStart":false})])]})]}),makeQuery(id+"F22.opExtrude","SWEPT_FACE",FACE,{"disambiguationData":[OSD([subQ3])]})]}),makeQuery(id+"F24.opExtrude","SWEPT_FACE",FACE,{"disambiguationData":[OSD([subQ0])]})]}),makeQuery(id+"F25.opExtrude","SWEPT_FACE",FACE,{"disambiguationData":[OSD([subQ5,subQ4,subQ3,sQuery(id+"F21.wireOp",EDGE,"E14.left")])]})]}),makeQuery(id+"F26.opExtrude","SWEPT_FACE",FACE,{"disambiguationData":[OSD([subQ2,subQ1,subQ0,sQuery(id+"F23.wireOp",EDGE,"E15.left")])]})]})});}
            var sketch = newSketch(context, id + "F32", { "sketchPlane" : qUnion([Q0])});
            skLineSegment(sketch, "E16", {"start": v(41.5, 0) * mm, "end": v(41.5, 30.47) * mm, "construction": true});
            skLineSegment(sketch, "E17.bottom", {"start": v(74.13, 3.43) * mm, "end": v(54.13, 3.43) * mm});
            skLineSegment(sketch, "E17.top", {"start": v(74.13, 0) * mm, "end": v(54.13, 0) * mm});
            skLineSegment(sketch, "E17.left", {"start": v(74.13, 3.43) * mm, "end": v(74.13, 0) * mm});
            skLineSegment(sketch, "E17.right", {"start": v(54.13, 3.43) * mm, "end": v(54.13, 0) * mm});
            skLineSegment(sketch, "E18.MirrorCS", {"start": v(8.87, 3.43) * mm, "end": v(8.87, 0) * mm});
            skLineSegment(sketch, "E19.MirrorCS", {"start": v(8.87, 3.43) * mm, "end": v(28.87, 3.43) * mm});
            skLineSegment(sketch, "E20.MirrorCS", {"start": v(28.87, 3.43) * mm, "end": v(28.87, 0) * mm});
            skLineSegment(sketch, "E21.MirrorCS", {"start": v(8.87, 0) * mm, "end": v(28.87, 0) * mm});
            skSolve(sketch);
        }
        {
            var Q0;
            Q0=makeQuery(id+"F32.imprint","IMPRINT",FACE,{"disambiguationData":[TD([[makeQuery(id+"F32.imprint","IMPRINT",EDGE,{"derivedFrom":sQuery(id+"F32.wireOp",EDGE,"E17.bottom")}),-1.0]])]});
            var Q1;
            Q1=makeQuery(id+"F32.imprint","IMPRINT",FACE,{"disambiguationData":[TD([[makeQuery(id+"F32.imprint","IMPRINT",EDGE,{"derivedFrom":sQuery(id+"F32.wireOp",EDGE,"E18.MirrorCS")}),1.0]])]});
            extrude(context, id + "F33", {"entities" : qUnion([Q0, Q1]), "operationType" : NewBodyOperationType.ADD, "depth" : 15 * mm});
        }
        {
            var Q0;
            Q0=makeQuery(id+"F33.opExtrude","CAP_EDGE",EDGE,{"disambiguationData":[OSD([sQuery(id+"F32.wireOp",EDGE,"E17.left")])],"isStart":true});
            var Q1;
            Q1=makeQuery(id+"F33.opExtrude","CAP_EDGE",EDGE,{"disambiguationData":[OSD([sQuery(id+"F32.wireOp",EDGE,"E17.left")])],"isStart":false});
            var Q2;
            Q2=makeQuery(id+"F33.opExtrude","CAP_EDGE",EDGE,{"disambiguationData":[OSD([sQuery(id+"F32.wireOp",EDGE,"E17.right")])],"isStart":false});
            var Q3;
            Q3=makeQuery(id+"F33.opExtrude","CAP_EDGE",EDGE,{"disambiguationData":[OSD([sQuery(id+"F32.wireOp",EDGE,"E17.right")])],"isStart":true});
            var Q4;
            Q4=makeQuery(id+"F33.opExtrude","CAP_EDGE",EDGE,{"disambiguationData":[OSD([sQuery(id+"F32.wireOp",EDGE,"E20.MirrorCS")])],"isStart":true});
            var Q5;
            Q5=makeQuery(id+"F33.opExtrude","CAP_EDGE",EDGE,{"disambiguationData":[OSD([sQuery(id+"F32.wireOp",EDGE,"E20.MirrorCS")])],"isStart":false});
            var Q6;
            Q6=makeQuery(id+"F33.opExtrude","CAP_EDGE",EDGE,{"disambiguationData":[OSD([sQuery(id+"F32.wireOp",EDGE,"E18.MirrorCS")])],"isStart":false});
            var Q7;
            Q7=makeQuery(id+"F33.opExtrude","CAP_EDGE",EDGE,{"disambiguationData":[OSD([sQuery(id+"F32.wireOp",EDGE,"E18.MirrorCS")])],"isStart":true});
            fillet(context, id + "F34", {"entities" : qUnion([Q0, Q1, Q2, Q3, Q4, Q5, Q6, Q7]), "radius" : 5 * mm, "tangentPropagation" : true, "allowEdgeOverflow" : false});
        }
        {
            var Q0;
            {var subQ0=sQuery(id+"F0.wireOp",EDGE,"E0.right");var subQ1=sQuery(id+"F0.wireOp",EDGE,"E0.top");var subQ7=makeQuery(id+"F1.opExtrude","SWEPT_FACE",FACE,{"disambiguationData":[OSD([subQ1])]});var subQ9=makeQuery(id+"F5.opExtrude","SWEPT_FACE",FACE,{"disambiguationData":[OSD([sQuery(id+"F4.wireOp",EDGE,"E4.left")])]});Q0=makeQuery(id+"F25.boolean.opBoolean","MERGE",FACE,{"derivedFrom":[makeQuery(id+"F16.boolean.opBoolean","MERGE",FACE,{"derivedFrom":[makeQuery(id+"F13.boolean.opBoolean","MERGE",FACE,{"derivedFrom":[makeQuery(id+"F7.boolean.opBoolean","MERGE",FACE,{"derivedFrom":[makeQuery(id+"F5.boolean.opBoolean","SPLIT",FACE,{"disambiguationData":[TD([subQ9])],"derivedFrom":subQ7}),makeQuery(id+"F7.opExtrude","SWEPT_FACE",FACE,{"disambiguationData":[OSD([subQ1]),TDD([makeQuery(id+"F5.boolean.opBoolean","SPLIT",EDGE,{"disambiguationData":[TD([subQ9])],"derivedFrom":makeQuery(id+"F1.opExtrude","CAP_EDGE",EDGE,{"disambiguationData":[OSD([subQ1])],"isStart":true})})])]})]}),makeQuery(id+"F13.opExtrude","SWEPT_FACE",FACE,{"disambiguationData":[OSD([subQ1]),TDD([makeQuery(id+"F5.boolean.opBoolean","SPLIT",EDGE,{"disambiguationData":[TD([subQ9])],"derivedFrom":makeQuery(id+"F1.opExtrude","CAP_EDGE",EDGE,{"disambiguationData":[OSD([subQ1])],"isStart":false})})])]})]}),makeQuery(id+"F16.opExtrude","SWEPT_FACE",FACE,{"disambiguationData":[OSD([subQ1,subQ0])]})]}),makeQuery(id+"F25.opExtrude","SWEPT_FACE",FACE,{"disambiguationData":[OSD([subQ1,subQ0])]})]});}
            var sketch = newSketch(context, id + "F35", { "sketchPlane" : qUnion([Q0])});
            skText(sketch, "E22", { "text": "MILLER", "fontName": "RobotoSlab-Regular.ttf"});
            skText(sketch, "E23", { "text": "MADE", "fontName": "RobotoSlab-Regular.ttf"});
            const initialGuessF35  = {"E22": [-0.0825, 0.02102, 1, 0, 0.00697], "E23": [-0.03307, 0.02102, 1, 0, 0.00714]};
            skSetInitialGuess(sketch, initialGuessF35);
            skSolve(sketch);
        }
        {
            var Q0;
            Q0 = qSketchRegion(id + "F35", true);
            extrude(context, id + "F36", {"entities" : qUnion([Q0]), "operationType" : NewBodyOperationType.ADD, "depth" : .5 * mm});
        }
    });
